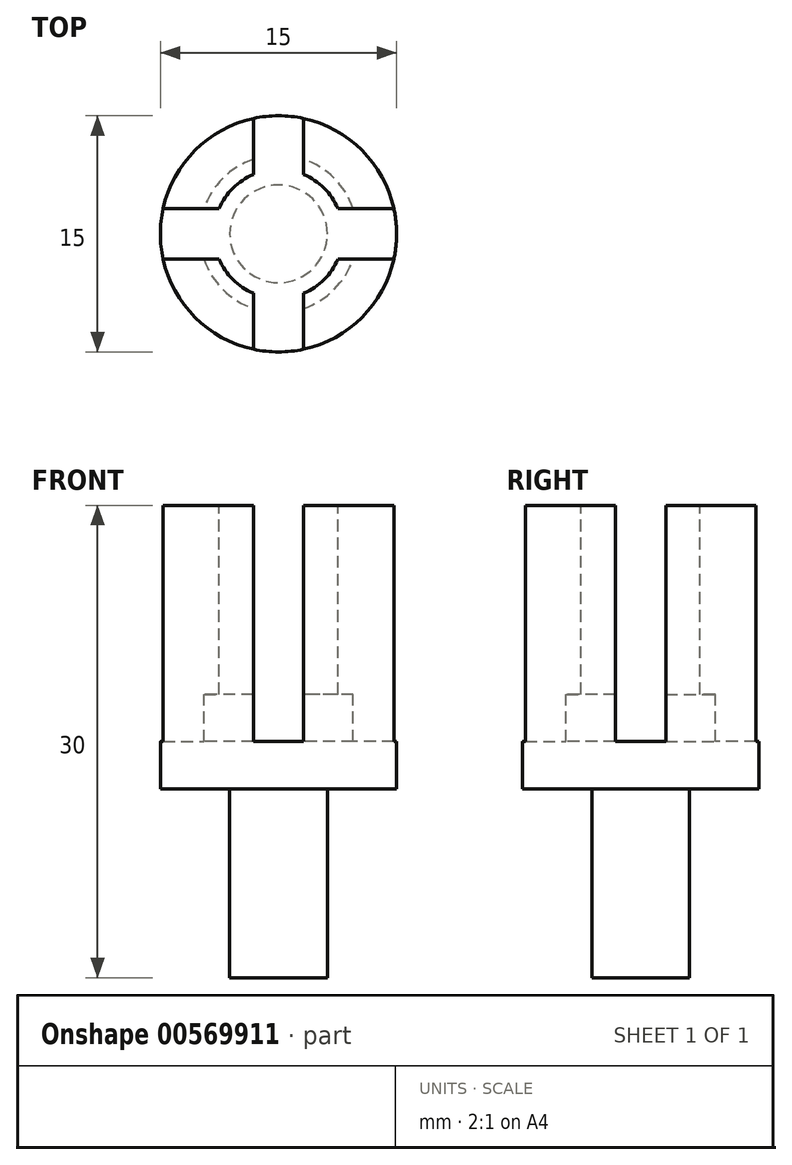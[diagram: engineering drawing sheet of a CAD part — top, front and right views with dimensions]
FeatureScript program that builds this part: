
annotation { "Feature Type Name" : "Feature", "Feature Type Description" : "" }
export const myFeature = defineFeature(function(context is Context, id is Id, definition is map)
    precondition{}
    {
        {
            var Q0;
            Q0=qCreatedBy(makeId("Front.planeOp"),FACE);
            var sketch = newSketch(context, id + "F0", { "sketchPlane" : qUnion([Q0])});
            skLineSegment(sketch, "E0", {"start": v(0, 0) * mm, "end": v(-3.1, 0) * mm});
            skLineSegment(sketch, "E1", {"start": v(-3.1, 0) * mm, "end": v(-3.1, 12) * mm});
            skLineSegment(sketch, "E2", {"start": v(-3.1, 12) * mm, "end": v(-7.5, 12) * mm});
            skLineSegment(sketch, "E3", {"start": v(-7.5, 12) * mm, "end": v(-7.5, 30) * mm});
            skLineSegment(sketch, "E4", {"start": v(-7.5, 30) * mm, "end": v(-4.1, 30) * mm});
            skLineSegment(sketch, "E5", {"start": v(0, 15) * mm, "end": v(0, 0) * mm});
            skLineSegment(sketch, "E6", {"start": v(-4.1, 30) * mm, "end": v(-4.1, 18) * mm});
            skLineSegment(sketch, "E7", {"start": v(-4.1, 18) * mm, "end": v(-5, 18) * mm});
            skLineSegment(sketch, "E8", {"start": v(-5, 18) * mm, "end": v(-5, 15) * mm});
            skLineSegment(sketch, "E9", {"start": v(-5, 15) * mm, "end": v(0, 15) * mm});
            skSolve(sketch);
        }
        {
            var Q0;
            Q0=qSketchRegion(id+"F0",true);
            var Q1;
            Q1=sQuery(id+"F0.wireOp",EDGE,"E5");
            revolve(context, id + "F1", {"entities" : qUnion([Q0]), "axis" : qUnion([Q1]), "revolveType" : RevolveType.FULL});
        }
        {
            var Q0;
            Q0=makeQuery(id+"F1.opRevolve","SWEPT_FACE",FACE,{"disambiguationData":[OSD([sQuery(id+"F0.wireOp",EDGE,"E4")])]});
            var sketch = newSketch(context, id + "F2", { "sketchPlane" : qUnion([Q0])});
            skLineSegment(sketch, "E10", {"start": v(-1.6, 10.17) * mm, "end": v(-1.6, 3.17) * mm});
            skLineSegment(sketch, "E11", {"start": v(1.6, 10.17) * mm, "end": v(1.6, 3.17) * mm});
            skLineSegment(sketch, "E12", {"start": v(-1.6, 10.17) * mm, "end": v(1.6, 10.17) * mm});
            skLineSegment(sketch, "E13", {"start": v(-1.6, 3.17) * mm, "end": v(1.6, 3.17) * mm});
            skLineSegment(sketch, "E14.1.0", {"start": v(-10.17, -1.6) * mm, "end": v(-10.17, 1.6) * mm});
            skLineSegment(sketch, "E14.1.1", {"start": v(-10.17, -1.6) * mm, "end": v(-3.17, -1.6) * mm});
            skLineSegment(sketch, "E14.1.2", {"start": v(-10.17, 1.6) * mm, "end": v(-3.17, 1.6) * mm});
            skLineSegment(sketch, "E14.1.3", {"start": v(-3.17, -1.6) * mm, "end": v(-3.17, 1.6) * mm});
            skLineSegment(sketch, "E14.2.0", {"start": v(1.6, -10.17) * mm, "end": v(-1.6, -10.17) * mm});
            skLineSegment(sketch, "E14.2.1", {"start": v(1.6, -10.17) * mm, "end": v(1.6, -3.17) * mm});
            skLineSegment(sketch, "E14.2.2", {"start": v(-1.6, -10.17) * mm, "end": v(-1.6, -3.17) * mm});
            skLineSegment(sketch, "E14.2.3", {"start": v(1.6, -3.17) * mm, "end": v(-1.6, -3.17) * mm});
            skLineSegment(sketch, "E14.3.0", {"start": v(10.17, 1.6) * mm, "end": v(10.17, -1.6) * mm});
            skLineSegment(sketch, "E14.3.1", {"start": v(10.17, 1.6) * mm, "end": v(3.17, 1.6) * mm});
            skLineSegment(sketch, "E14.3.2", {"start": v(10.17, -1.6) * mm, "end": v(3.17, -1.6) * mm});
            skLineSegment(sketch, "E14.3.3", {"start": v(3.17, 1.6) * mm, "end": v(3.17, -1.6) * mm});
            skPoint(sketch, "E14.center", {"position": v(0, 0) * mm});
            skSolve(sketch);
        }
        {
            var Q0;
            Q0=qSketchRegion(id+"F2",true);
            extrude(context, id + "F3", {"entities" : qUnion([Q0]), "operationType" : NewBodyOperationType.REMOVE, "oppositeDirection" : true, "depth" : 15 * mm, "offsetDistance" : 25 * mm});
        }
    });
